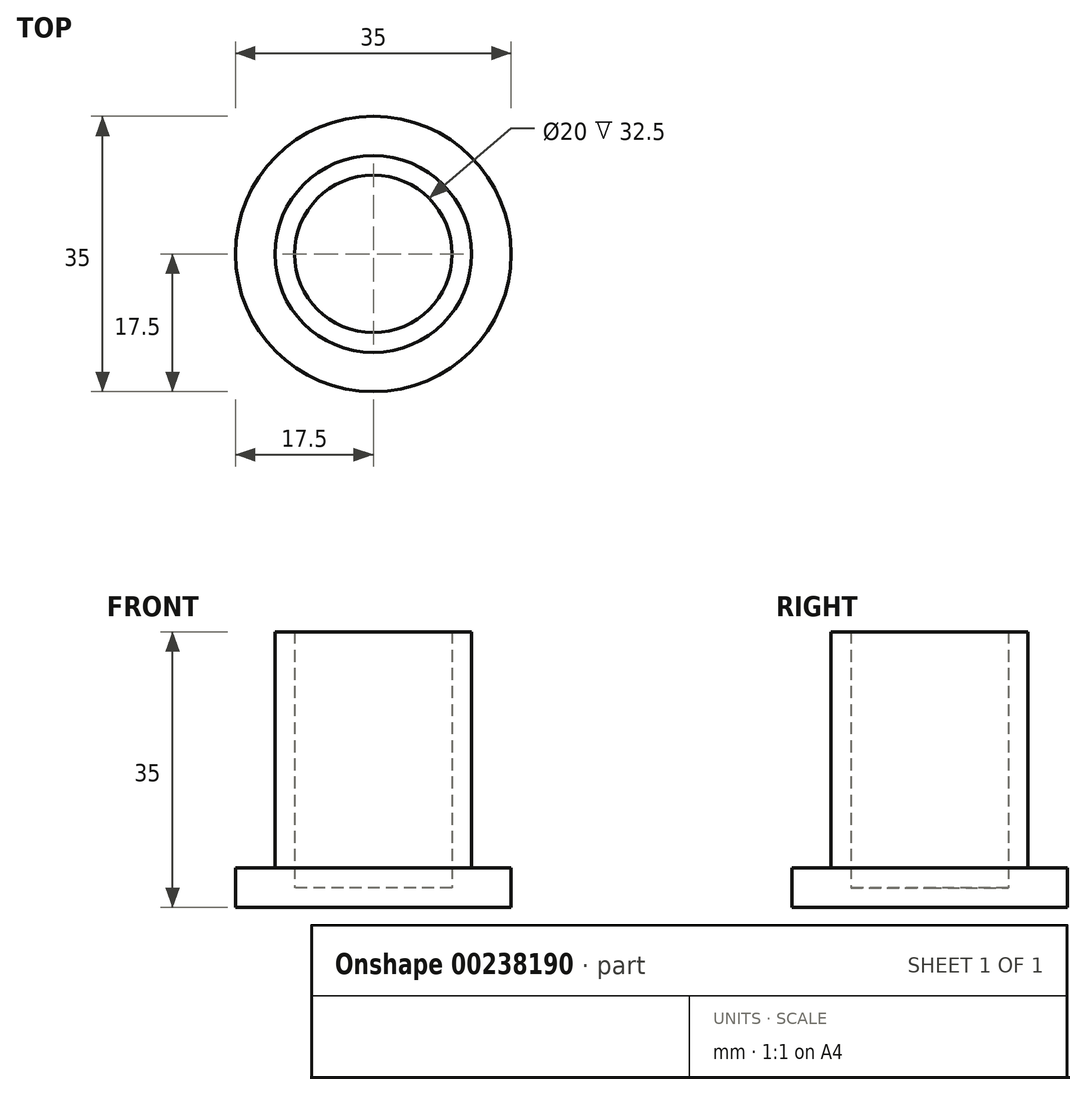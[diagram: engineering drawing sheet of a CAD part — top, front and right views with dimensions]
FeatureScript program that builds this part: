
annotation { "Feature Type Name" : "Feature", "Feature Type Description" : "" }
export const myFeature = defineFeature(function(context is Context, id is Id, definition is map)
    precondition{}
    {
        {
            var Q0;
            Q0=qCreatedBy(makeId("Top.planeOp"),FACE);
            var sketch = newSketch(context, id + "F0", { "sketchPlane" : qUnion([Q0])});
            skCircle(sketch, "E0", {"center": v(0, 0) * mm, "radius": 17.5 * mm});
            skSolve(sketch);
        }
        {
            var Q0;
            Q0=makeQuery(id+"F0.imprint","IMPRINT",FACE,{"disambiguationData":[TD([[makeQuery(id+"F0.imprint","IMPRINT",EDGE,{"derivedFrom":sQuery(id+"F0.wireOp",EDGE,"E0")}),1.0]])]});
            extrude(context, id + "F1", {"entities" : qUnion([Q0]), "depth" : 5 * mm, "offsetDistance" : 25 * mm});
        }
        {
            var Q0;
            Q0=makeQuery(id+"F1.opExtrude","CAP_FACE",FACE,{"disambiguationData":[OSD([sQuery(id+"F0.wireOp",EDGE,"E0")])],"isStart":false});
            var sketch = newSketch(context, id + "F2", { "sketchPlane" : qUnion([Q0])});
            skCircle(sketch, "E1", {"center": v(0, 0) * mm, "radius": 12.5 * mm});
            skSolve(sketch);
        }
        {
            var Q0;
            Q0 = qSketchRegion(id + "F2", true);
            extrude(context, id + "F3", {"entities" : qUnion([Q0]), "operationType" : NewBodyOperationType.ADD, "depth" : 30 * mm, "offsetDistance" : 25 * mm});
        }
        {
            var Q0;
            Q0=makeQuery(id+"F3.opExtrude","CAP_FACE",FACE,{"disambiguationData":[OSD([sQuery(id+"F2.wireOp",EDGE,"E1")])],"isStart":false});
            shell(context, id + "F4", {"entities" : qUnion([Q0]), "thickness" : 2.5 * mm});
        }
    });
